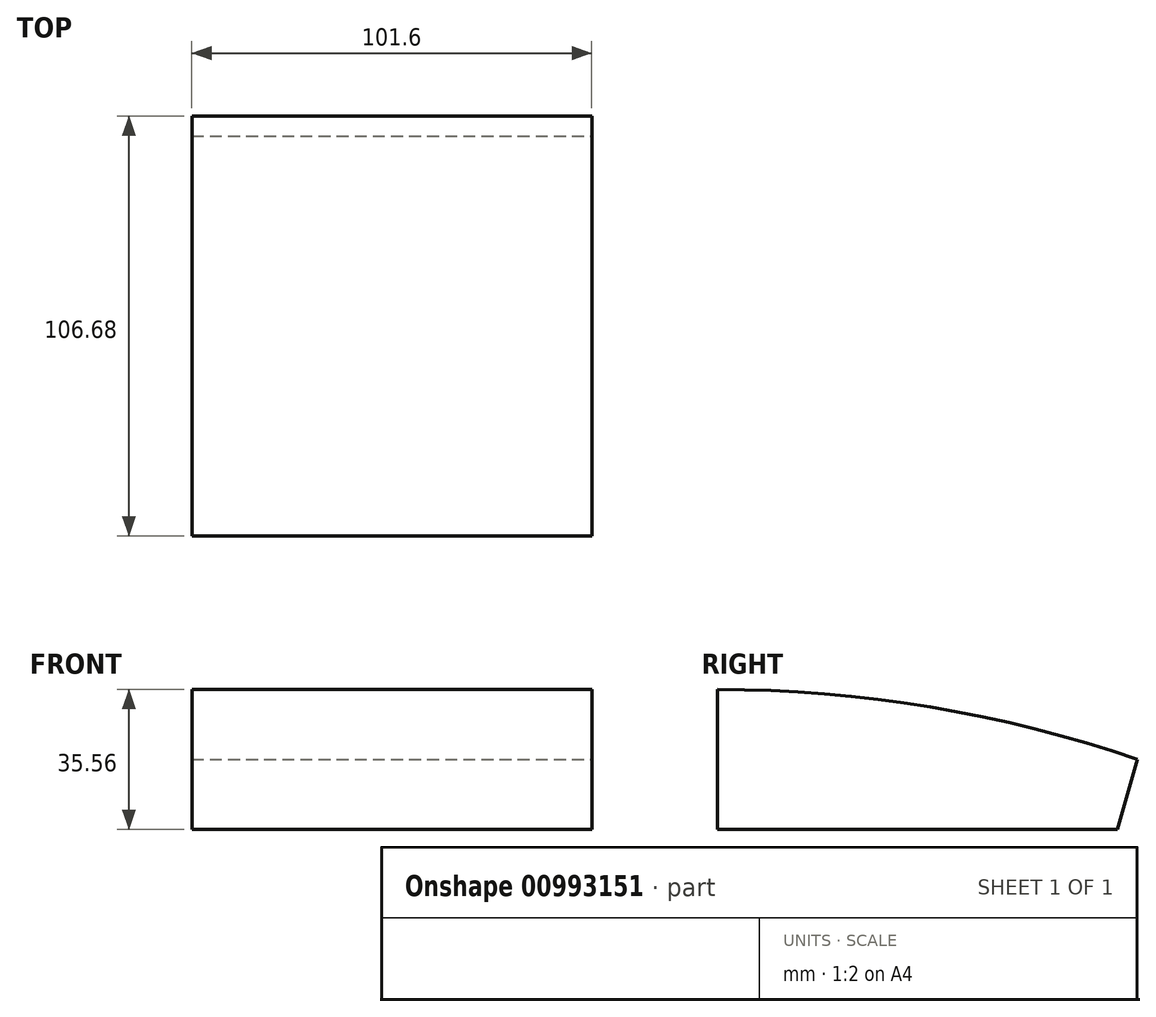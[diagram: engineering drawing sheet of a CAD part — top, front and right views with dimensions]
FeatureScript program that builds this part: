
annotation { "Feature Type Name" : "Feature", "Feature Type Description" : "" }
export const myFeature = defineFeature(function(context is Context, id is Id, definition is map)
    precondition{}
    {
        {
            var Q0;
            Q0=qCreatedBy(makeId("Top.planeOp"),FACE);
            var sketch = newSketch(context, id + "F0", { "sketchPlane" : qUnion([Q0])});
            skLineSegment(sketch, "E0.bottom", {"start": v(-53.08, 81.42) * mm, "end": v(48.52, 81.42) * mm});
            skLineSegment(sketch, "E0.top", {"start": v(-53.08, -25.26) * mm, "end": v(48.52, -25.26) * mm});
            skLineSegment(sketch, "E0.left", {"start": v(-53.08, 81.42) * mm, "end": v(-53.08, -25.26) * mm});
            skLineSegment(sketch, "E0.right", {"start": v(48.52, 81.42) * mm, "end": v(48.52, -25.26) * mm});
            skSolve(sketch);
        }
        {
            var Q0;
            Q0=makeQuery(id+"F0.imprint","IMPRINT",FACE,{"disambiguationData":[TD([[makeQuery(id+"F0.imprint","IMPRINT",EDGE,{"derivedFrom":sQuery(id+"F0.wireOp",EDGE,"E0.bottom")}),-1.0]])]});
            extrude(context, id + "F1", {"entities" : qUnion([Q0]), "depth" : 35.56 * mm, "offsetDistance" : 25.4 * mm});
        }
        {
            var Q0;
            Q0=makeQuery(id+"F1.opExtrude","SWEPT_FACE",FACE,{"disambiguationData":[OSD([sQuery(id+"F0.wireOp",EDGE,"E0.right")])]});
            var sketch = newSketch(context, id + "F2", { "sketchPlane" : qUnion([Q0])});
            skArc(sketch, "E1", {"start": v(81.42, 17.78) * mm, "mid": v(28.81, 31.08) * mm, "end": v(-25.26, 35.56) * mm});
            skLineSegment(sketch, "E2", {"start": v(81.42, 17.78) * mm, "end": v(76.34, 0) * mm});
            skSolve(sketch);
        }
        {
            var Q0;
            {var subQ0=sQuery(id+"F2.wireOp",EDGE,"E1");Q0=makeQuery(id+"F2.imprint","IMPRINT",FACE,{"disambiguationData":[TD([[makeQuery(id+"F2.imprint","IMPRINT",EDGE,{"derivedFrom":subQ0}),-1.0]])]});}
            var Q1;
            {var subQ0=sQuery(id+"F2.wireOp",EDGE,"E2");Q1=makeQuery(id+"F2.imprint","IMPRINT",FACE,{"disambiguationData":[TD([[makeQuery(id+"F2.imprint","IMPRINT",EDGE,{"derivedFrom":subQ0}),1.0]])]});}
            extrude(context, id + "F3", {"entities" : qUnion([Q0, Q1]), "operationType" : NewBodyOperationType.REMOVE, "oppositeDirection" : true, "depth" : 127 * mm, "offsetDistance" : 25.4 * mm});
        }
    });
